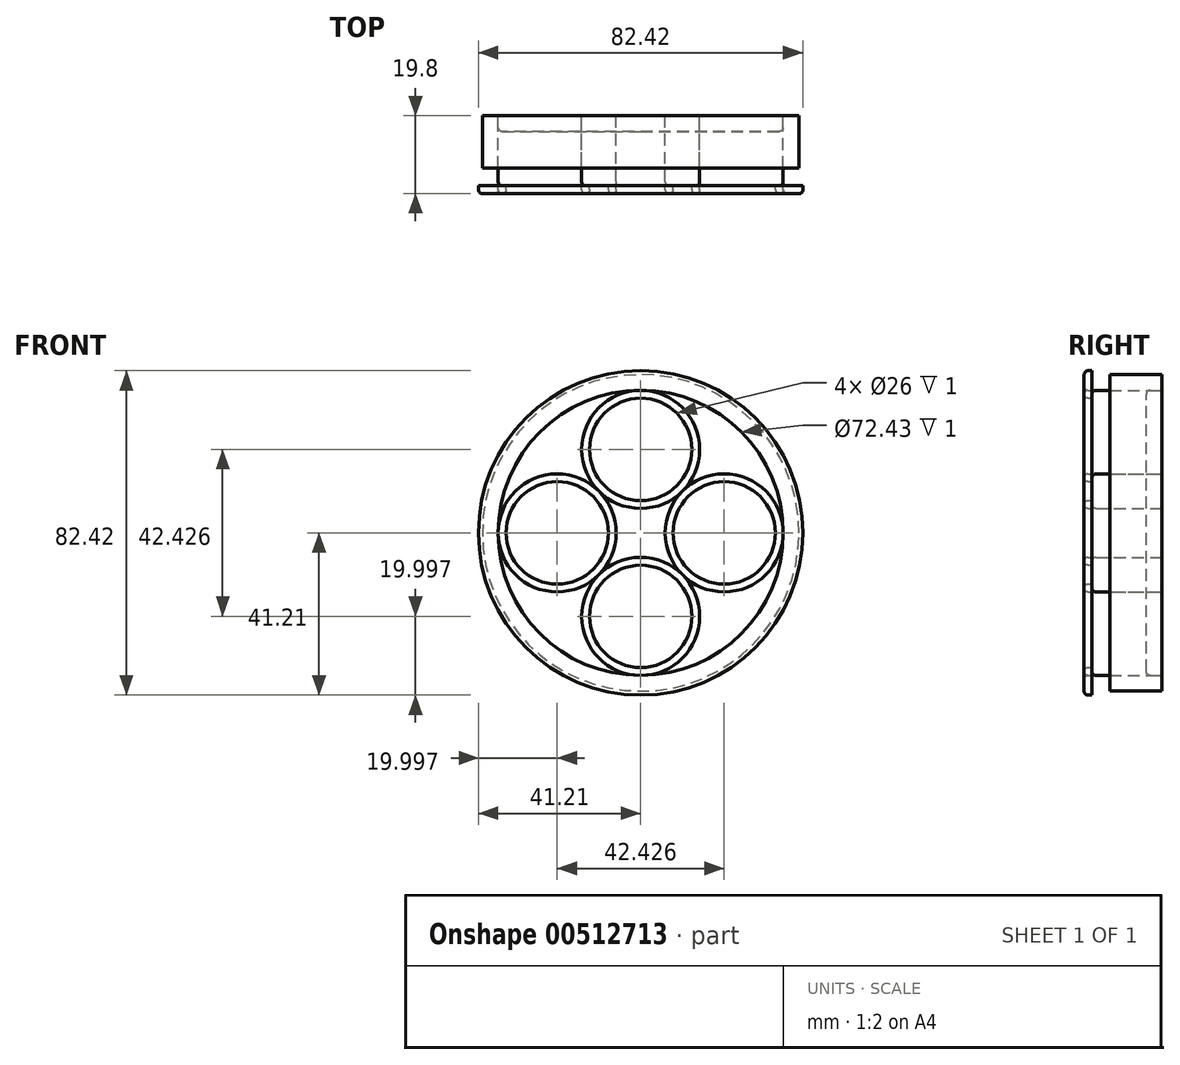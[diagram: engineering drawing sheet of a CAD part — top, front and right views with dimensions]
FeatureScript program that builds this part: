
annotation { "Feature Type Name" : "Feature", "Feature Type Description" : "" }
export const myFeature = defineFeature(function(context is Context, id is Id, definition is map)
    precondition{}
    {
        {
            var Q0;
            Q0=qCreatedBy(makeId("Front.planeOp"),FACE);
            var sketch = newSketch(context, id + "F0", { "sketchPlane" : qUnion([Q0])});
            skCircle(sketch, "E0.cCircle", {"center": v(0, 0) * mm, "radius": 15 * mm, "construction": true});
            skLineSegment(sketch, "E0.0", {"start": v(0, 21.21) * mm, "end": v(21.21, 0) * mm, "construction": true});
            skLineSegment(sketch, "E0.1", {"start": v(21.21, 0) * mm, "end": v(0, -21.21) * mm, "construction": true});
            skLineSegment(sketch, "E0.2", {"start": v(0, -21.21) * mm, "end": v(-21.21, 0) * mm, "construction": true});
            skLineSegment(sketch, "E0.3", {"start": v(-21.21, 0) * mm, "end": v(0, 21.21) * mm, "construction": true});
            skPoint(sketch, "E0.0.midPoint", {"position": v(10.6, 10.6) * mm});
            skLineSegment(sketch, "E1", {"start": v(0, 0) * mm, "end": v(0, 42.43) * mm, "construction": true});
            skCircle(sketch, "E2", {"center": v(0, 21.21) * mm, "radius": 15 * mm});
            skCircle(sketch, "E3", {"center": v(21.21, 0) * mm, "radius": 15 * mm});
            skCircle(sketch, "E4", {"center": v(0, -21.21) * mm, "radius": 15 * mm});
            skCircle(sketch, "E5", {"center": v(-21.21, 0) * mm, "radius": 15 * mm});
            skCircle(sketch, "E6", {"center": v(0, 0) * mm, "radius": 36.21 * mm});
            skSolve(sketch);
        }
        {
            var Q0;
            {var subQ0=sQuery(id+"F0.wireOp",EDGE,"E6");var subQ1=sQuery(id+"F0.wireOp",EDGE,"E2");var subQ2=makeQuery(id+"F0.imprint","INTERSECT",VERTEX,{"derivedFrom":[subQ1,subQ0]});Q0=makeQuery(id+"F0.imprint","IMPRINT",FACE,{"disambiguationData":[TD([[makeQuery(id+"F0.imprint","IMPRINT",EDGE,{"disambiguationData":[TD([[subQ2,-1.0]])],"derivedFrom":subQ1}),-1.0]])]});}
            var Q1;
            {var subQ0=sQuery(id+"F0.wireOp",EDGE,"E2");var subQ1=makeQuery(id+"F0.imprint","INTERSECT",VERTEX,{"derivedFrom":[subQ0,sQuery(id+"F0.wireOp",EDGE,"E6")]});Q1=makeQuery(id+"F0.imprint","IMPRINT",FACE,{"disambiguationData":[TD([[makeQuery(id+"F0.imprint","IMPRINT",EDGE,{"disambiguationData":[TD([[subQ1,-1.0]])],"derivedFrom":subQ0}),1.0]])]});}
            var Q2;
            {var subQ0=sQuery(id+"F0.wireOp",EDGE,"E6");var subQ1=sQuery(id+"F0.wireOp",EDGE,"E2");var subQ2=makeQuery(id+"F0.imprint","INTERSECT",VERTEX,{"derivedFrom":[subQ1,subQ0]});Q2=makeQuery(id+"F0.imprint","IMPRINT",FACE,{"disambiguationData":[TD([[makeQuery(id+"F0.imprint","IMPRINT",EDGE,{"disambiguationData":[TD([[subQ2,1.0]])],"derivedFrom":subQ1}),-1.0]])]});}
            var Q3;
            {var subQ0=sQuery(id+"F0.wireOp",EDGE,"E3");var subQ1=makeQuery(id+"F0.imprint","INTERSECT",VERTEX,{"derivedFrom":[subQ0,sQuery(id+"F0.wireOp",EDGE,"E6")]});Q3=makeQuery(id+"F0.imprint","IMPRINT",FACE,{"disambiguationData":[TD([[makeQuery(id+"F0.imprint","IMPRINT",EDGE,{"disambiguationData":[TD([[subQ1,-1.0]])],"derivedFrom":subQ0}),1.0]])]});}
            var Q4;
            {var subQ0=sQuery(id+"F0.wireOp",EDGE,"E6");var subQ1=sQuery(id+"F0.wireOp",EDGE,"E3");var subQ2=makeQuery(id+"F0.imprint","INTERSECT",VERTEX,{"derivedFrom":[subQ1,subQ0]});Q4=makeQuery(id+"F0.imprint","IMPRINT",FACE,{"disambiguationData":[TD([[makeQuery(id+"F0.imprint","IMPRINT",EDGE,{"disambiguationData":[TD([[subQ2,1.0]])],"derivedFrom":subQ1}),-1.0]])]});}
            var Q5;
            {var subQ0=sQuery(id+"F0.wireOp",EDGE,"E4");var subQ1=makeQuery(id+"F0.imprint","INTERSECT",VERTEX,{"derivedFrom":[sQuery(id+"F0.wireOp",EDGE,"E3"),subQ0]});Q5=makeQuery(id+"F0.imprint","IMPRINT",FACE,{"disambiguationData":[TD([[makeQuery(id+"F0.imprint","IMPRINT",EDGE,{"disambiguationData":[TD([[subQ1,-1.0]])],"derivedFrom":subQ0}),1.0]])]});}
            var Q6;
            {var subQ0=sQuery(id+"F0.wireOp",EDGE,"E6");var subQ1=sQuery(id+"F0.wireOp",EDGE,"E4");var subQ2=makeQuery(id+"F0.imprint","INTERSECT",VERTEX,{"derivedFrom":[subQ1,subQ0]});Q6=makeQuery(id+"F0.imprint","IMPRINT",FACE,{"disambiguationData":[TD([[makeQuery(id+"F0.imprint","IMPRINT",EDGE,{"disambiguationData":[TD([[subQ2,1.0]])],"derivedFrom":subQ1}),-1.0]])]});}
            var Q7;
            {var subQ0=sQuery(id+"F0.wireOp",EDGE,"E5");var subQ1=makeQuery(id+"F0.imprint","INTERSECT",VERTEX,{"derivedFrom":[subQ0,sQuery(id+"F0.wireOp",EDGE,"E6")]});Q7=makeQuery(id+"F0.imprint","IMPRINT",FACE,{"disambiguationData":[TD([[makeQuery(id+"F0.imprint","IMPRINT",EDGE,{"disambiguationData":[TD([[subQ1,1.0]])],"derivedFrom":subQ0}),1.0]])]});}
            var Q8;
            {var subQ0=sQuery(id+"F0.wireOp",EDGE,"E5");var subQ1=sQuery(id+"F0.wireOp",EDGE,"E2");var subQ2=makeQuery(id+"F0.imprint","INTERSECT",VERTEX,{"derivedFrom":[subQ1,subQ0]});Q8=makeQuery(id+"F0.imprint","IMPRINT",FACE,{"disambiguationData":[TD([[makeQuery(id+"F0.imprint","IMPRINT",EDGE,{"disambiguationData":[TD([[subQ2,-1.0]])],"derivedFrom":subQ1}),-1.0]])]});}
            extrude(context, id + "F1", {"entities" : qUnion([Q0, Q1, Q2, Q3, Q4, Q5, Q6, Q7, Q8]), "depth" : 4 * mm});
        }
        {
            var Q0;
            {var subQ0=sQuery(id+"F0.wireOp",EDGE,"E5");var subQ1=makeQuery(id+"F0.imprint","INTERSECT",VERTEX,{"derivedFrom":[subQ0,sQuery(id+"F0.wireOp",EDGE,"E6")]});Q0=makeQuery(id+"F0.imprint","IMPRINT",FACE,{"disambiguationData":[TD([[makeQuery(id+"F0.imprint","IMPRINT",EDGE,{"disambiguationData":[TD([[subQ1,1.0]])],"derivedFrom":subQ0}),1.0]])]});}
            var Q1;
            {var subQ0=sQuery(id+"F0.wireOp",EDGE,"E2");var subQ1=makeQuery(id+"F0.imprint","INTERSECT",VERTEX,{"derivedFrom":[subQ0,sQuery(id+"F0.wireOp",EDGE,"E6")]});Q1=makeQuery(id+"F0.imprint","IMPRINT",FACE,{"disambiguationData":[TD([[makeQuery(id+"F0.imprint","IMPRINT",EDGE,{"disambiguationData":[TD([[subQ1,-1.0]])],"derivedFrom":subQ0}),1.0]])]});}
            var Q2;
            {var subQ0=sQuery(id+"F0.wireOp",EDGE,"E3");var subQ1=makeQuery(id+"F0.imprint","INTERSECT",VERTEX,{"derivedFrom":[subQ0,sQuery(id+"F0.wireOp",EDGE,"E6")]});Q2=makeQuery(id+"F0.imprint","IMPRINT",FACE,{"disambiguationData":[TD([[makeQuery(id+"F0.imprint","IMPRINT",EDGE,{"disambiguationData":[TD([[subQ1,-1.0]])],"derivedFrom":subQ0}),1.0]])]});}
            var Q3;
            {var subQ0=sQuery(id+"F0.wireOp",EDGE,"E4");var subQ1=makeQuery(id+"F0.imprint","INTERSECT",VERTEX,{"derivedFrom":[sQuery(id+"F0.wireOp",EDGE,"E3"),subQ0]});Q3=makeQuery(id+"F0.imprint","IMPRINT",FACE,{"disambiguationData":[TD([[makeQuery(id+"F0.imprint","IMPRINT",EDGE,{"disambiguationData":[TD([[subQ1,-1.0]])],"derivedFrom":subQ0}),1.0]])]});}
            extrude(context, id + "F2", {"entities" : qUnion([Q0, Q1, Q2, Q3]), "depth" : 17.8 * mm});
        }
        {
            var Q0;
            Q0=makeQuery(id+"F2.opExtrude","CAP_FACE",FACE,{"disambiguationData":[OSD([sQuery(id+"F0.wireOp",EDGE,"E5")])],"isStart":false});
            var Q1;
            Q1=makeQuery(id+"F2.opExtrude","CAP_FACE",FACE,{"disambiguationData":[OSD([sQuery(id+"F0.wireOp",EDGE,"E2")])],"isStart":false});
            var Q2;
            Q2=makeQuery(id+"F2.opExtrude","CAP_FACE",FACE,{"disambiguationData":[OSD([sQuery(id+"F0.wireOp",EDGE,"E3")])],"isStart":false});
            var Q3;
            Q3=makeQuery(id+"F2.opExtrude","CAP_FACE",FACE,{"disambiguationData":[OSD([sQuery(id+"F0.wireOp",EDGE,"E4")])],"isStart":false});
            var Q4;
            Q4=makeQuery(id+"F1.opExtrude","CAP_FACE",FACE,{"disambiguationData":[OSD([sQuery(id+"F0.wireOp",EDGE,"E6")])],"isStart":false});
            fillet(context, id + "F3", {"entities" : qUnion([Q0, Q1, Q2, Q3, Q4]), "radius" : 1 * mm, "tangentPropagation" : true, "allowEdgeOverflow" : false});
        }
        {
            var Q0;
            Q0=makeQuery(id+"F2.opExtrude","CAP_FACE",FACE,{"disambiguationData":[OSD([sQuery(id+"F0.wireOp",EDGE,"E5")])],"isStart":false});
            var sketch = newSketch(context, id + "F4", { "sketchPlane" : qUnion([Q0])});
            skCircle(sketch, "E7.0", {"center": v(0, 21.21) * mm, "radius": 15 * mm});
            skCircle(sketch, "E8.0", {"center": v(-21.21, 0) * mm, "radius": 15 * mm});
            skCircle(sketch, "E9.0", {"center": v(0, -21.21) * mm, "radius": 15 * mm});
            skCircle(sketch, "E10.0", {"center": v(21.21, 0) * mm, "radius": 15 * mm});
            skCircle(sketch, "E11.0", {"center": v(0, 21.21) * mm, "radius": 13 * mm});
            skCircle(sketch, "E12.0", {"center": v(-21.21, 0) * mm, "radius": 13 * mm});
            skCircle(sketch, "E13.0", {"center": v(0, -21.21) * mm, "radius": 13 * mm});
            skCircle(sketch, "E14.0", {"center": v(21.21, 0) * mm, "radius": 13 * mm});
            skCircle(sketch, "E15.0", {"center": v(0, 0) * mm, "radius": 41.21 * mm});
            skCircle(sketch, "E16.0", {"center": v(0, 0) * mm, "radius": 36.21 * mm});
            skSolve(sketch);
        }
        {
            var Q0;
            Q0 = qSketchRegion(id + "F4", true);
            var Q1;
            {var subQ0=sQuery(id+"F4.wireOp",EDGE,"E8.0");var subQ1=makeQuery(id+"F4.imprint","INTERSECT",VERTEX,{"derivedFrom":[subQ0,sQuery(id+"F4.wireOp",EDGE,"E16.0")]});Q1=makeQuery(id+"F4.imprint","IMPRINT",FACE,{"disambiguationData":[TD([[makeQuery(id+"F4.imprint","IMPRINT",EDGE,{"disambiguationData":[TD([[subQ1,1.0]])],"derivedFrom":subQ0}),1.0]])]});}
            var Q2;
            Q2=makeQuery(id+"F4.imprint","IMPRINT",FACE,{"disambiguationData":[TD([[makeQuery(id+"F4.imprint","IMPRINT",EDGE,{"derivedFrom":sQuery(id+"F4.wireOp",EDGE,"E12.0")}),-1.0]])]});
            var Q3;
            Q3=makeQuery(id+"F4.imprint","IMPRINT",FACE,{"disambiguationData":[TD([[makeQuery(id+"F4.imprint","IMPRINT",EDGE,{"derivedFrom":sQuery(id+"F4.wireOp",EDGE,"E11.0")}),-1.0]])]});
            var Q4;
            {var subQ0=sQuery(id+"F4.wireOp",EDGE,"E7.0");var subQ1=makeQuery(id+"F4.imprint","INTERSECT",VERTEX,{"derivedFrom":[subQ0,sQuery(id+"F4.wireOp",EDGE,"E16.0")]});Q4=makeQuery(id+"F4.imprint","IMPRINT",FACE,{"disambiguationData":[TD([[makeQuery(id+"F4.imprint","IMPRINT",EDGE,{"disambiguationData":[TD([[subQ1,1.0]])],"derivedFrom":subQ0}),1.0]])]});}
            var Q5;
            Q5=makeQuery(id+"F4.imprint","IMPRINT",FACE,{"disambiguationData":[TD([[makeQuery(id+"F4.imprint","IMPRINT",EDGE,{"derivedFrom":sQuery(id+"F4.wireOp",EDGE,"E14.0")}),-1.0]])]});
            var Q6;
            {var subQ0=sQuery(id+"F4.wireOp",EDGE,"E10.0");var subQ1=makeQuery(id+"F4.imprint","INTERSECT",VERTEX,{"derivedFrom":[subQ0,sQuery(id+"F4.wireOp",EDGE,"E16.0")]});Q6=makeQuery(id+"F4.imprint","IMPRINT",FACE,{"disambiguationData":[TD([[makeQuery(id+"F4.imprint","IMPRINT",EDGE,{"disambiguationData":[TD([[subQ1,1.0]])],"derivedFrom":subQ0}),1.0]])]});}
            var Q7;
            Q7=makeQuery(id+"F4.imprint","IMPRINT",FACE,{"disambiguationData":[TD([[makeQuery(id+"F4.imprint","IMPRINT",EDGE,{"derivedFrom":sQuery(id+"F4.wireOp",EDGE,"E13.0")}),-1.0]])]});
            var Q8;
            {var subQ0=sQuery(id+"F4.wireOp",EDGE,"E9.0");var subQ1=makeQuery(id+"F4.imprint","INTERSECT",VERTEX,{"derivedFrom":[subQ0,sQuery(id+"F4.wireOp",EDGE,"E16.0")]});Q8=makeQuery(id+"F4.imprint","IMPRINT",FACE,{"disambiguationData":[TD([[makeQuery(id+"F4.imprint","IMPRINT",EDGE,{"disambiguationData":[TD([[subQ1,-1.0]])],"derivedFrom":subQ0}),1.0]])]});}
            extrude(context, id + "F5", {"entities" : qUnion([Q0, Q1, Q2, Q3, Q4, Q5, Q6, Q7, Q8]), "depth" : 2 * mm});
        }
        {
            var Q0;
            Q0=makeQuery(id+"F5.opExtrude","CAP_FACE",FACE,{"disambiguationData":[OSD([sQuery(id+"F4.wireOp",EDGE,"E8.0"),sQuery(id+"F4.wireOp",EDGE,"E12.0")])],"isStart":false});
            var Q1;
            Q1=makeQuery(id+"F5.opExtrude","CAP_FACE",FACE,{"disambiguationData":[OSD([sQuery(id+"F4.wireOp",EDGE,"E7.0"),sQuery(id+"F4.wireOp",EDGE,"E11.0")])],"isStart":false});
            var Q2;
            Q2=makeQuery(id+"F5.opExtrude","CAP_FACE",FACE,{"disambiguationData":[OSD([sQuery(id+"F4.wireOp",EDGE,"E10.0"),sQuery(id+"F4.wireOp",EDGE,"E14.0")])],"isStart":false});
            var Q3;
            Q3=makeQuery(id+"F5.opExtrude","CAP_FACE",FACE,{"disambiguationData":[OSD([sQuery(id+"F4.wireOp",EDGE,"E9.0"),sQuery(id+"F4.wireOp",EDGE,"E13.0")])],"isStart":false});
            var Q4;
            Q4=makeQuery(id+"F5.opExtrude","CAP_FACE",FACE,{"disambiguationData":[OSD([sQuery(id+"F4.wireOp",EDGE,"E15.0"),sQuery(id+"F4.wireOp",EDGE,"E16.0")])],"isStart":false});
            fillet(context, id + "F6", {"entities" : qUnion([Q0, Q1, Q2, Q3, Q4]), "radius" : 1 * mm, "tangentPropagation" : true, "allowEdgeOverflow" : false});
        }
        {
            var Q0;
            Q0=qCreatedBy(makeId("Front.planeOp"),FACE);
            var sketch = newSketch(context, id + "F7", { "sketchPlane" : qUnion([Q0])});
            skCircle(sketch, "E17.0.0", {"center": v(0, 0) * mm, "radius": 40.21 * mm});
            skSolve(sketch);
        }
        {
            var Q0;
            Q0=makeQuery(id+"F7.imprint","IMPRINT",FACE,{"disambiguationData":[TD([[makeQuery(id+"F7.imprint","IMPRINT",EDGE,{"derivedFrom":sQuery(id+"F7.wireOp",EDGE,"E17.0.0")}),1.0]])]});
            extrude(context, id + "F8", {"entities" : qUnion([Q0]), "depth" : 13.3 * mm});
        }
    });
